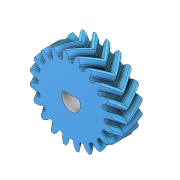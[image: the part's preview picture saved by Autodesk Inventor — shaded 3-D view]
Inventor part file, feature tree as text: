
AUTODESK INVENTOR PART (.ipt)
format: ipt  version: 2020.3 (Build 243373000, 373)  size: 1,525,248 bytes
history: native  units: mm
features: extrude x1, sketch x1, imported_body x1
ambient origin geometry x8: Origin, YZ Plane, XZ Plane, XY Plane, X Axis, Y Axis, Z Axis, Center Point
bodies: Solid1 (feature_tree)
feature tree (3):
  extrude  "Extrusion1"  [1 undecoded]
  sketch  "Sketch1"  dims[d0=86.0mm d1=0.0mm]
  imported_body  "Base1"
note: 1 required parameter value undecoded (feature->parameter linkage not recoverable at this tier; creation-order binding heuristic only, values carry confidence <= 0.55)
